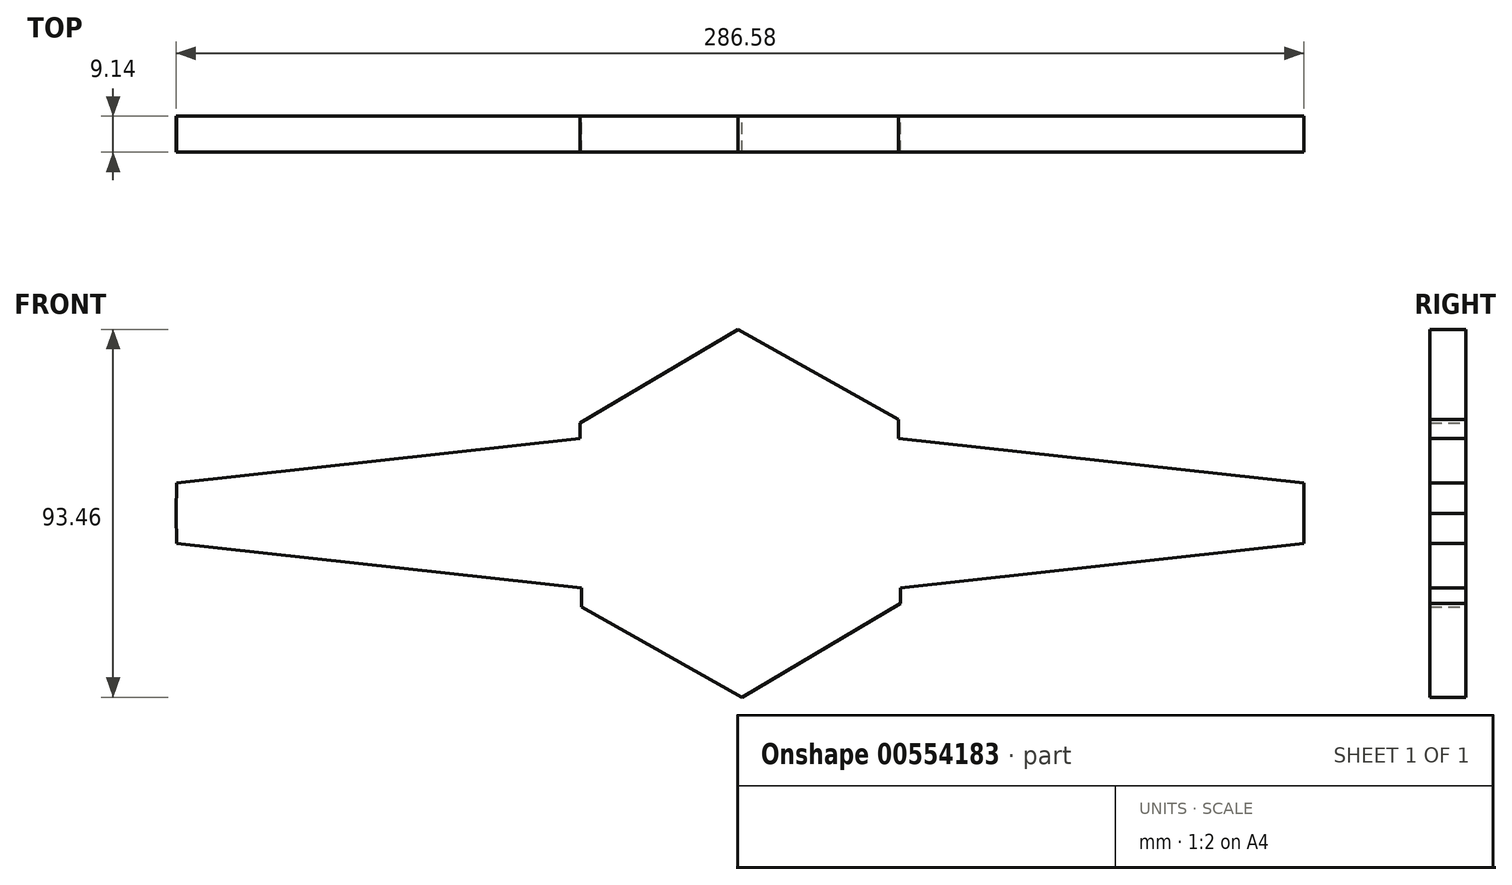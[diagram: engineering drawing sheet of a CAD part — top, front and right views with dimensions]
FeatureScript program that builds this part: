
annotation { "Feature Type Name" : "Feature", "Feature Type Description" : "" }
export const myFeature = defineFeature(function(context is Context, id is Id, definition is map)
    precondition{}
    {
        {
            var Q0;
            Q0=qCreatedBy(makeId("Front.planeOp"),FACE);
            var sketch = newSketch(context, id + "F0", { "sketchPlane" : qUnion([Q0])});
            skLineSegment(sketch, "E0.0", {"start": v(40.71, -22.95) * mm, "end": v(0.48, -46.73) * mm});
            skLineSegment(sketch, "E0.1", {"start": v(0.48, -46.73) * mm, "end": v(-40.23, -23.78) * mm});
            skLineSegment(sketch, "E0.2", {"start": v(-40.23, -23.78) * mm, "end": v(-40.28, -19.02) * mm});
            skLineSegment(sketch, "E0.3", {"start": v(-40.71, 22.95) * mm, "end": v(-0.48, 46.73) * mm});
            skLineSegment(sketch, "E0.4", {"start": v(-0.48, 46.73) * mm, "end": v(40.23, 23.78) * mm});
            skLineSegment(sketch, "E0.5", {"start": v(40.23, 23.78) * mm, "end": v(40.28, 19.02) * mm});
            skPoint(sketch, "E0.0.midPoint", {"position": v(20.6, -34.84) * mm});
            skLineSegment(sketch, "E1", {"start": v(40.28, 19.02) * mm, "end": v(143.2, 7.68) * mm});
            skLineSegment(sketch, "E2", {"start": v(143.2, 7.68) * mm, "end": v(143.29, 0) * mm});
            skLineSegment(sketch, "E3.MirrorCS", {"start": v(40.28, -19.02) * mm, "end": v(143.2, -7.68) * mm});
            skLineSegment(sketch, "E4.MirrorCS", {"start": v(143.2, -7.68) * mm, "end": v(143.29, 0) * mm});
            skLineSegment(sketch, "E5.MirrorCS", {"start": v(-40.28, 19.02) * mm, "end": v(-143.2, 7.68) * mm});
            skLineSegment(sketch, "E6.MirrorCS", {"start": v(-40.28, -19.02) * mm, "end": v(-143.2, -7.68) * mm});
            skLineSegment(sketch, "E7.MirrorCS", {"start": v(-143.2, -7.68) * mm, "end": v(-143.29, 0) * mm});
            skLineSegment(sketch, "E8.MirrorCS", {"start": v(-143.2, 7.68) * mm, "end": v(-143.29, 0) * mm});
            skLineSegment(sketch, "E9.trimOffspring", {"start": v(-40.67, 18.98) * mm, "end": v(-40.71, 22.95) * mm});
            skLineSegment(sketch, "E10.trimOffspring", {"start": v(40.67, -18.98) * mm, "end": v(40.71, -22.95) * mm});
            skSolve(sketch);
        }
        {
            var Q0;
            Q0=makeQuery(id+"F0.imprint","IMPRINT",FACE,{"disambiguationData":[TD([[makeQuery(id+"F0.imprint","IMPRINT",EDGE,{"derivedFrom":sQuery(id+"F0.wireOp",EDGE,"E0.0")}),-1.0]])]});
            extrude(context, id + "F1", {"entities" : qUnion([Q0]), "depth" : 9.14 * mm, "offsetDistance" : 25.4 * mm});
        }
    });
